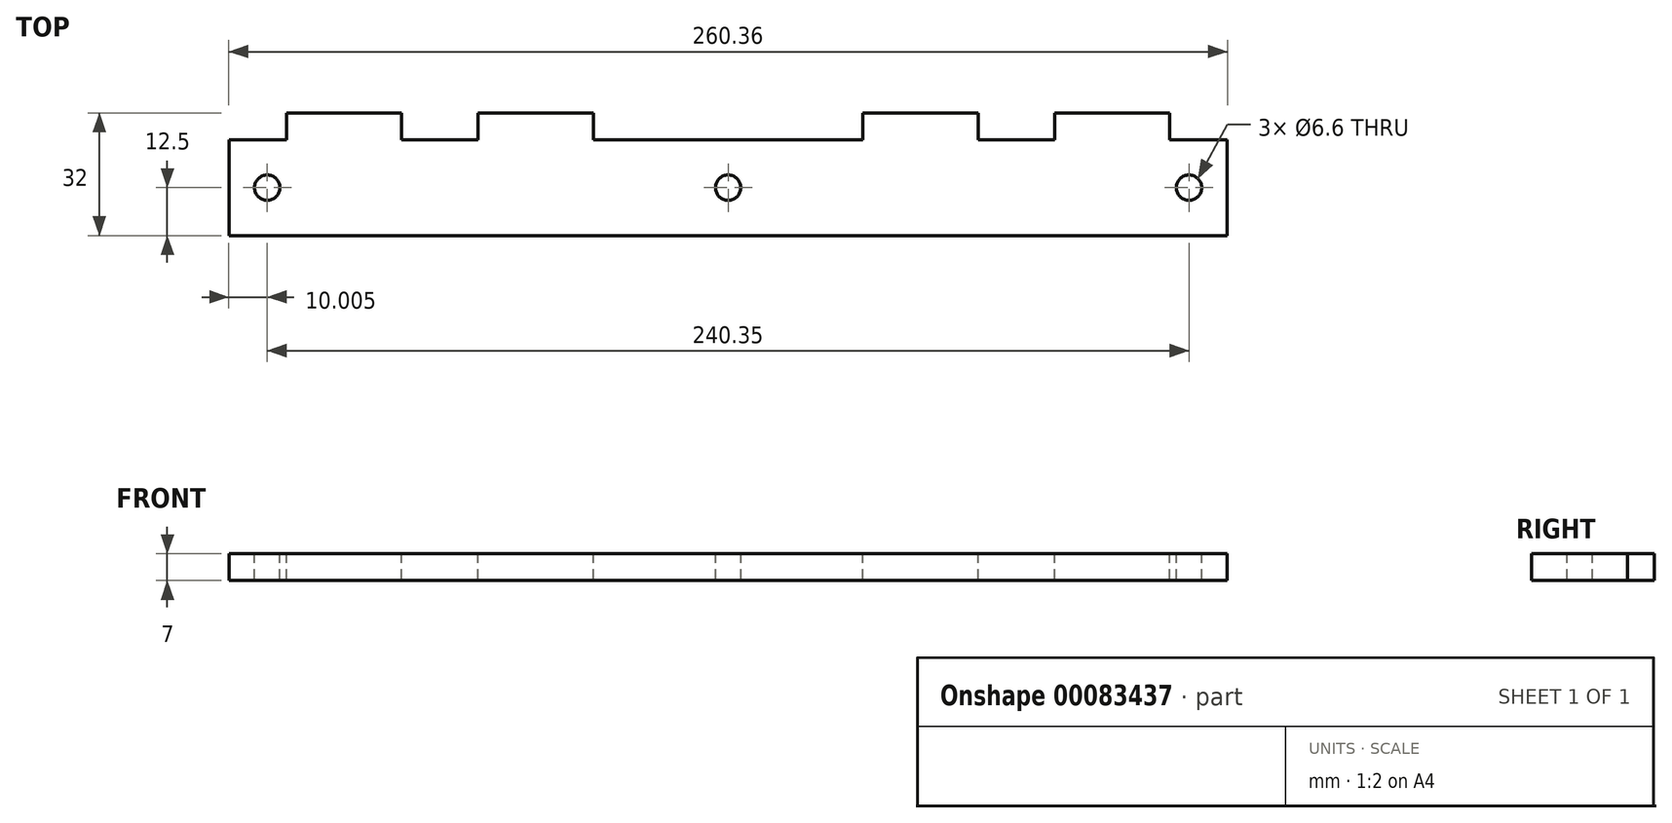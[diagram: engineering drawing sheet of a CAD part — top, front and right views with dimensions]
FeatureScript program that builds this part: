
annotation { "Feature Type Name" : "Feature", "Feature Type Description" : "" }
export const myFeature = defineFeature(function(context is Context, id is Id, definition is map)
    precondition{}
    {
        {
            var Q0;
            Q0=qCreatedBy(makeId("Top.planeOp"),FACE);
            var sketch = newSketch(context, id + "F0", { "sketchPlane" : qUnion([Q0])});
            skLineSegment(sketch, "E0.bottom", {"start": v(-130.18, 12.5) * mm, "end": v(130.18, 12.5) * mm});
            skLineSegment(sketch, "E0.top", {"start": v(-130.18, -12.5) * mm, "end": v(130.18, -12.5) * mm});
            skLineSegment(sketch, "E0.left", {"start": v(-130.18, 12.5) * mm, "end": v(-130.18, -12.5) * mm});
            skLineSegment(sketch, "E0.right", {"start": v(130.18, 12.5) * mm, "end": v(130.18, -12.5) * mm});
            skPoint(sketch, "E0.middle", {"position": v(0, 0) * mm});
            skSolve(sketch);
        }
        {
            var Q0;
            Q0=qSketchRegion(id+"F0",true);
            extrude(context, id + "F1", {"entities" : qUnion([Q0]), "depth" : 7 * mm});
        }
        {
            var Q0;
            Q0=makeQuery(id+"F1.opExtrude","CAP_FACE",FACE,{"disambiguationData":[OSD([sQuery(id+"F0.wireOp",EDGE,"E0.bottom"),sQuery(id+"F0.wireOp",EDGE,"E0.top"),sQuery(id+"F0.wireOp",EDGE,"E0.left"),sQuery(id+"F0.wireOp",EDGE,"E0.right")])],"isStart":false});
            var sketch = newSketch(context, id + "F2", { "sketchPlane" : qUnion([Q0])});
            skLineSegment(sketch, "E1", {"start": v(-130.18, 0) * mm, "end": v(130.18, 0) * mm, "construction": true});
            skCircle(sketch, "E2", {"center": v(-120.18, 0) * mm, "radius": 3.3 * mm});
            skCircle(sketch, "E3", {"center": v(0, 0) * mm, "radius": 3.3 * mm});
            skCircle(sketch, "E4", {"center": v(120.18, 0) * mm, "radius": 3.3 * mm});
            skSolve(sketch);
        }
        {
            var Q0;
            Q0=qSketchRegion(id+"F2",true);
            extrude(context, id + "F3", {"entities" : qUnion([Q0]), "operationType" : NewBodyOperationType.REMOVE, "endBound" : BoundingType.UP_TO_NEXT, "oppositeDirection" : true, "depth" : 25 * mm});
        }
        {
            var Q0;
            Q0=makeQuery(id+"F1.opExtrude","SWEPT_FACE",FACE,{"disambiguationData":[OSD([sQuery(id+"F0.wireOp",EDGE,"E0.bottom")])]});
            var sketch = newSketch(context, id + "F4", { "sketchPlane" : qUnion([Q0])});
            skLineSegment(sketch, "E5.bottom", {"start": v(115.18, 0) * mm, "end": v(85.18, 0) * mm});
            skLineSegment(sketch, "E5.top", {"start": v(115.18, 7) * mm, "end": v(85.18, 7) * mm});
            skLineSegment(sketch, "E5.left", {"start": v(115.18, 0) * mm, "end": v(115.18, 7) * mm});
            skLineSegment(sketch, "E5.right", {"start": v(85.18, 0) * mm, "end": v(85.18, 7) * mm});
            skLineSegment(sketch, "E6.bottom", {"start": v(65.18, 0) * mm, "end": v(35.18, 0) * mm});
            skLineSegment(sketch, "E6.top", {"start": v(65.18, 7) * mm, "end": v(35.18, 7) * mm});
            skLineSegment(sketch, "E6.left", {"start": v(65.18, 0) * mm, "end": v(65.18, 7) * mm});
            skLineSegment(sketch, "E6.right", {"start": v(35.18, 0) * mm, "end": v(35.18, 7) * mm});
            skLineSegment(sketch, "E7.bottom", {"start": v(-35.18, 0) * mm, "end": v(-65.18, 0) * mm});
            skLineSegment(sketch, "E7.top", {"start": v(-35.18, 7) * mm, "end": v(-65.18, 7) * mm});
            skLineSegment(sketch, "E7.left", {"start": v(-35.18, 0) * mm, "end": v(-35.18, 7) * mm});
            skLineSegment(sketch, "E7.right", {"start": v(-65.18, 0) * mm, "end": v(-65.18, 7) * mm});
            skLineSegment(sketch, "E8.bottom", {"start": v(-85.18, 0) * mm, "end": v(-115.18, 0) * mm});
            skLineSegment(sketch, "E8.top", {"start": v(-85.18, 7) * mm, "end": v(-115.18, 7) * mm});
            skLineSegment(sketch, "E8.left", {"start": v(-85.18, 0) * mm, "end": v(-85.18, 7) * mm});
            skLineSegment(sketch, "E8.right", {"start": v(-115.18, 0) * mm, "end": v(-115.18, 7) * mm});
            skSolve(sketch);
        }
        {
            var Q0;
            Q0 = qSketchRegion(id + "F4", true);
            extrude(context, id + "F5", {"entities" : qUnion([Q0]), "operationType" : NewBodyOperationType.ADD, "depth" : 7 * mm});
        }
    });
